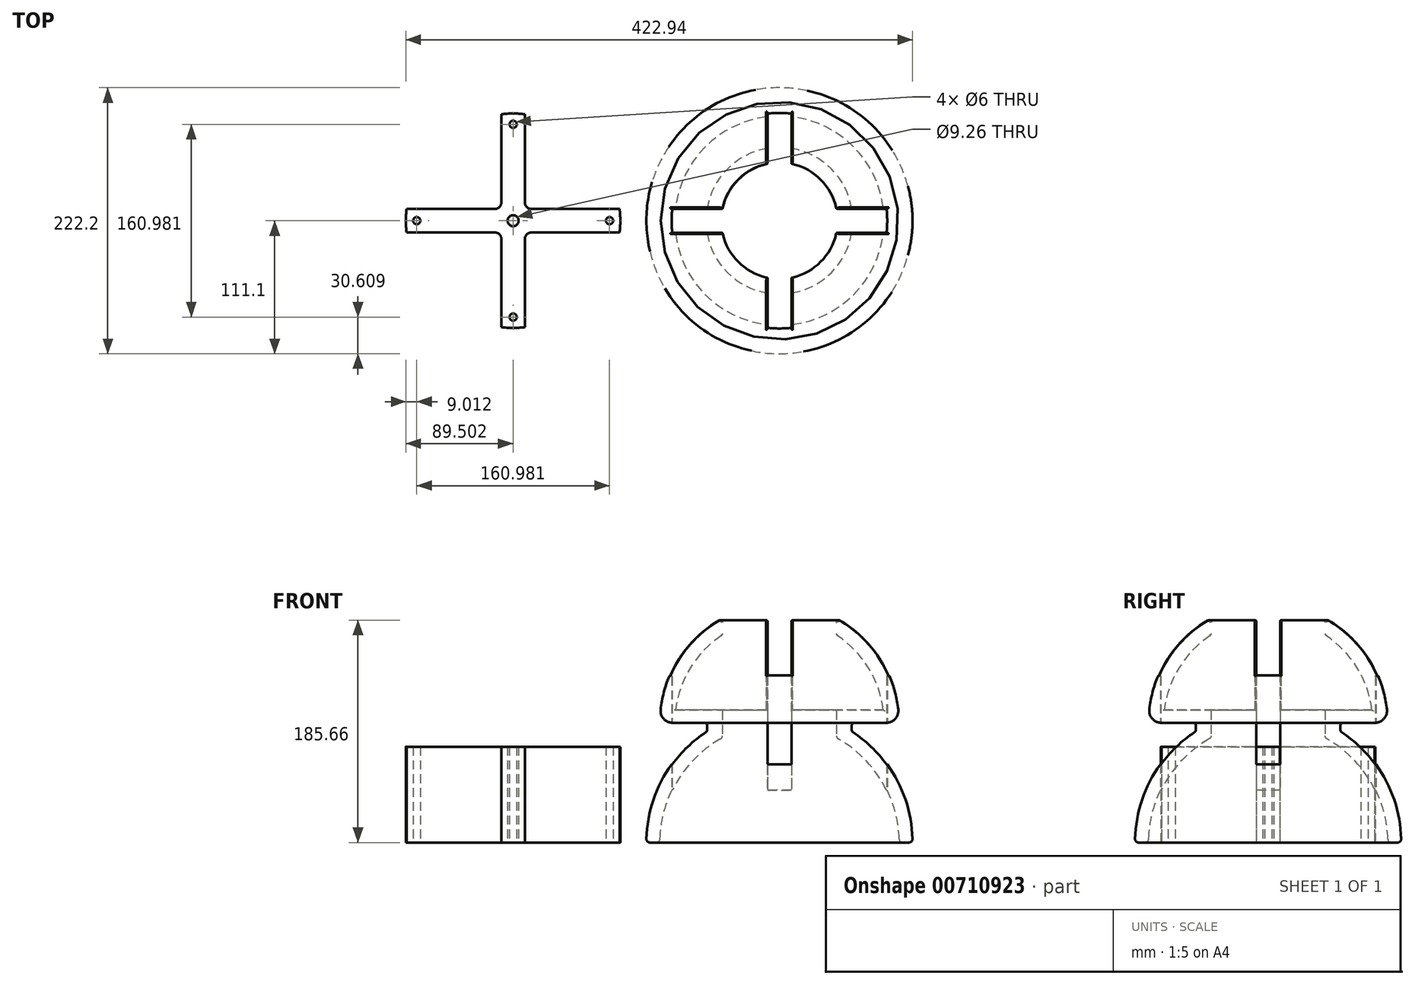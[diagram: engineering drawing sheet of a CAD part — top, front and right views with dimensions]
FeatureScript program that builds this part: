
annotation { "Feature Type Name" : "Feature", "Feature Type Description" : "" }
export const myFeature = defineFeature(function(context is Context, id is Id, definition is map)
    precondition{}
    {
        {
            var Q0;
            Q0=qCreatedBy(makeId("Front.planeOp"),FACE);
            var sketch = newSketch(context, id + "F0", { "sketchPlane" : qUnion([Q0])});
            skArc(sketch, "E0", {"start": v(100, 0) * mm, "mid": v(86.21, 50.67) * mm, "end": v(48.65, 87.37) * mm});
            skArc(sketch, "E1", {"start": v(111.14, 0) * mm, "mid": v(97.88, 52.66) * mm, "end": v(61.25, 92.74) * mm});
            skPoint(sketch, "E2", {"position": v(0, 100) * mm});
            skLineSegment(sketch, "E3", {"start": v(111.14, 0) * mm, "end": v(100, 0) * mm});
            skLineSegment(sketch, "E4", {"start": v(0, 0) * mm, "end": v(0, 246.19) * mm});
            skPoint(sketch, "E5.orphan", {"position": v(-88.06, 100) * mm});
            skPoint(sketch, "E6.orphan", {"position": v(-99.8, 100) * mm});
            skPoint(sketch, "E7.orphan", {"position": v(-111.14, 0) * mm});
            skPoint(sketch, "E8.orphan", {"position": v(-100, 0) * mm});
            skPoint(sketch, "E9.startSnap0", {"position": v(61.25, 144.4) * mm});
            skPoint(sketch, "E10.orphan", {"position": v(35.1, 144.4) * mm});
            skPoint(sketch, "E11.orphan", {"position": v(88.06, 100) * mm});
            skPoint(sketch, "E12.orphan", {"position": v(87.39, 144.4) * mm});
            skPoint(sketch, "E13.start.orphan", {"position": v(99.8, 100) * mm});
            skArc(sketch, "E14", {"start": v(99.2, 110.84) * mm, "mid": v(83.2, 155.13) * mm, "end": v(48.65, 187.14) * mm});
            skPoint(sketch, "E9.start.orphan", {"position": v(61.25, 133.56) * mm});
            skLineSegment(sketch, "E15", {"start": v(48.65, 87.37) * mm, "end": v(48.65, 110.84) * mm});
            skLineSegment(sketch, "E16", {"start": v(61.25, 92.74) * mm, "end": v(61.25, 100) * mm});
            skLineSegment(sketch, "E17", {"start": v(87.39, 110.84) * mm, "end": v(61.25, 110.84) * mm});
            skPoint(sketch, "E18.trimOffspring.end.orphan", {"position": v(-110.69, 100) * mm});
            skLineSegment(sketch, "E19", {"start": v(61.25, 110.84) * mm, "end": v(48.65, 110.84) * mm});
            skArc(sketch, "E20", {"start": v(87.39, 110.84) * mm, "mid": v(74.87, 146.36) * mm, "end": v(48.65, 173.4) * mm});
            skPoint(sketch, "E21.orphan", {"position": v(110.69, 100) * mm});
            skLineSegment(sketch, "E22", {"start": v(48.65, 187.14) * mm, "end": v(48.65, 173.4) * mm});
            skLineSegment(sketch, "E23", {"start": v(99.2, 110.84) * mm, "end": v(99.8, 100) * mm});
            skLineSegment(sketch, "E24", {"start": v(61.25, 100) * mm, "end": v(99.8, 100) * mm});
            skSolve(sketch);
        }
        {
            var Q0;
            Q0=makeQuery(id+"F0.imprint","IMPRINT",FACE,{"disambiguationData":[TD([[makeQuery(id+"F0.imprint","IMPRINT",EDGE,{"derivedFrom":sQuery(id+"F0.wireOp",EDGE,"E0")}),-1.0]])]});
            var Q1;
            Q1=sQuery(id+"F0.wireOp",EDGE,"E4");
            revolve(context, id + "F1", {"surfaceOperationType" : NewSurfaceOperationType.NEW, "entities" : qUnion([Q0]), "axis" : qUnion([Q1]), "revolveType" : RevolveType.FULL});
        }
        {
            var Q0;
            Q0=makeQuery(id+"F1.opRevolve","SWEPT_EDGE",EDGE,{"disambiguationData":[OSD([sQuery(id+"F0.wireOp",EDGE,"E20"),sQuery(id+"F0.wireOp",EDGE,"E22")])]});
            var Q1;
            Q1=makeQuery(id+"F1.opRevolve","SWEPT_EDGE",EDGE,{"disambiguationData":[OSD([sQuery(id+"F0.wireOp",EDGE,"E14"),sQuery(id+"F0.wireOp",EDGE,"E22")])]});
            fillet(context, id + "F2", {"entities" : qUnion([Q0, Q1]), "radius" : 2 * mm, "tangentPropagation" : true, "allowEdgeOverflow" : false});
        }
        {
            var Q0;
            Q0=makeQuery(id+"F1.opRevolve","SWEPT_FACE",FACE,{"disambiguationData":[OSD([sQuery(id+"F0.wireOp",EDGE,"E0")])]});
            var Q1;
            Q1=makeQuery(id+"F1.opRevolve","SWEPT_EDGE",EDGE,{"disambiguationData":[OSD([sQuery(id+"F0.wireOp",EDGE,"E1"),sQuery(id+"F0.wireOp",EDGE,"E3")])]});
            fillet(context, id + "F3", {"entities" : qUnion([Q0, Q1]), "radius" : 3 * mm, "tangentPropagation" : true, "allowEdgeOverflow" : false});
        }
        {
            var Q0;
            Q0=makeQuery(id+"F1.opRevolve","SWEPT_EDGE",EDGE,{"disambiguationData":[OSD([sQuery(id+"F0.wireOp",EDGE,"E16"),sQuery(id+"F0.wireOp",EDGE,"E24")])]});
            var Q1;
            Q1=makeQuery(id+"F1.opRevolve","SWEPT_EDGE",EDGE,{"disambiguationData":[OSD([sQuery(id+"F0.wireOp",EDGE,"E1"),sQuery(id+"F0.wireOp",EDGE,"E16")])]});
            fillet(context, id + "F4", {"entities" : qUnion([Q0, Q1]), "radius" : 2 * mm, "tangentPropagation" : true, "allowEdgeOverflow" : false});
        }
        {
            var Q0;
            Q0=qCreatedBy(makeId("Top.planeOp"),FACE);
            var sketch = newSketch(context, id + "F5", { "sketchPlane" : qUnion([Q0])});
            skArc(sketch, "E25", {"start": v(-89.44, 10) * mm, "mid": v(-90, 0) * mm, "end": v(-89.44, -10) * mm});
            skLineSegment(sketch, "E26", {"start": v(-10, -89.44) * mm, "end": v(-10, -10) * mm});
            skLineSegment(sketch, "E27", {"start": v(10, 89.44) * mm, "end": v(10, 10) * mm});
            skLineSegment(sketch, "E28", {"start": v(-89.44, 10) * mm, "end": v(-10, 10) * mm});
            skLineSegment(sketch, "E29", {"start": v(-89.44, -10) * mm, "end": v(-10, -10) * mm});
            skPoint(sketch, "E30.orphan", {"position": v(-59.43, -10) * mm});
            skPoint(sketch, "E31.orphan", {"position": v(10, -62.73) * mm});
            skPoint(sketch, "E32.orphan", {"position": v(-10, -60.97) * mm});
            skPoint(sketch, "E33.orphan", {"position": v(62.07, 10) * mm});
            skArc(sketch, "E34.trimOffspring", {"start": v(10, 89.44) * mm, "mid": v(0, 90) * mm, "end": v(-10, 89.44) * mm});
            skArc(sketch, "E35.trimOffspring", {"start": v(89.44, -10) * mm, "mid": v(90, 0) * mm, "end": v(89.44, 10) * mm});
            skArc(sketch, "E36.trimOffspring", {"start": v(-10, -89.44) * mm, "mid": v(0, -90) * mm, "end": v(10, -89.44) * mm});
            skLineSegment(sketch, "E37.trimOffspring", {"start": v(10, -10) * mm, "end": v(89.44, -10) * mm});
            skLineSegment(sketch, "E38.trimOffspring", {"start": v(10, 10) * mm, "end": v(89.44, 10) * mm});
            skLineSegment(sketch, "E39.trimOffspring", {"start": v(10, -10) * mm, "end": v(10, -89.44) * mm});
            skLineSegment(sketch, "E40.trimOffspring", {"start": v(-10, 10) * mm, "end": v(-10, 89.44) * mm});
            skSolve(sketch);
        }
        {
            var Q0;
            Q0=makeQuery(id+"F1.opRevolve","SWEPT_EDGE",EDGE,{"disambiguationData":[OSD([sQuery(id+"F0.wireOp",EDGE,"E23"),sQuery(id+"F0.wireOp",EDGE,"E24")])]});
            fillet(context, id + "F6", {"entities" : qUnion([Q0]), "radius" : 10 * mm, "tangentPropagation" : true, "allowEdgeOverflow" : false});
        }
        {
            var Q0;
            Q0=makeQuery(id+"F5.imprint","IMPRINT",FACE,{"disambiguationData":[TD([[makeQuery(id+"F5.imprint","IMPRINT",EDGE,{"derivedFrom":sQuery(id+"F5.wireOp",EDGE,"E25")}),1.0]])]});
            extrude(context, id + "F7", {"entities" : qUnion([Q0]), "operationType" : NewBodyOperationType.REMOVE, "depth" : 210 * mm, "offsetDistance" : 25 * mm});
        }
        {
            var Q0;
            Q0=makeQuery(id+"F7.boolean.opBoolean","INTERSECT",EDGE,{"derivedFrom":[makeQuery(id+"F1.opRevolve","SWEPT_FACE",FACE,{"disambiguationData":[OSD([sQuery(id+"F0.wireOp",EDGE,"E14")])]}),makeQuery(id+"F7.opExtrude","SWEPT_FACE",FACE,{"disambiguationData":[OSD([sQuery(id+"F5.wireOp",EDGE,"E25")])]})]});
            var Q1;
            Q1=makeQuery(id+"F7.boolean.opBoolean","INTERSECT",EDGE,{"derivedFrom":[makeQuery(id+"F1.opRevolve","SWEPT_FACE",FACE,{"disambiguationData":[OSD([sQuery(id+"F0.wireOp",EDGE,"E14")])]}),makeQuery(id+"F7.opExtrude","SWEPT_FACE",FACE,{"disambiguationData":[OSD([sQuery(id+"F5.wireOp",EDGE,"E28")])]})]});
            var Q2;
            Q2=makeQuery(id+"F1.opRevolve","SWEPT_FACE",FACE,{"disambiguationData":[OSD([sQuery(id+"F0.wireOp",EDGE,"E14")])]});
            var Q3;
            Q3=makeQuery(id+"F7.boolean.opBoolean","INTERSECT",EDGE,{"derivedFrom":[makeQuery(id+"F1.opRevolve","SWEPT_FACE",FACE,{"disambiguationData":[OSD([sQuery(id+"F0.wireOp",EDGE,"E17"),sQuery(id+"F0.wireOp",EDGE,"E19")])]}),makeQuery(id+"F7.opExtrude","SWEPT_FACE",FACE,{"disambiguationData":[OSD([sQuery(id+"F5.wireOp",EDGE,"E40.trimOffspring")])]})]});
            var Q4;
            Q4=makeQuery(id+"F7.boolean.opBoolean","INTERSECT",EDGE,{"derivedFrom":[makeQuery(id+"F1.opRevolve","SWEPT_FACE",FACE,{"disambiguationData":[OSD([sQuery(id+"F0.wireOp",EDGE,"E17"),sQuery(id+"F0.wireOp",EDGE,"E19")])]}),makeQuery(id+"F7.opExtrude","SWEPT_FACE",FACE,{"disambiguationData":[OSD([sQuery(id+"F5.wireOp",EDGE,"E34.trimOffspring")])]})]});
            var Q5;
            Q5=makeQuery(id+"F7.boolean.opBoolean","INTERSECT",EDGE,{"derivedFrom":[makeQuery(id+"F1.opRevolve","SWEPT_FACE",FACE,{"disambiguationData":[OSD([sQuery(id+"F0.wireOp",EDGE,"E17"),sQuery(id+"F0.wireOp",EDGE,"E19")])]}),makeQuery(id+"F7.opExtrude","SWEPT_FACE",FACE,{"disambiguationData":[OSD([sQuery(id+"F5.wireOp",EDGE,"E27")])]})]});
            var Q6;
            {var subQ0=sQuery(id+"F0.wireOp",EDGE,"E15");var subQ1=sQuery(id+"F0.wireOp",EDGE,"E19");Q6=makeQuery(id+"F7.boolean.opBoolean","SPLIT",EDGE,{"disambiguationData":[TD([makeQuery(id+"F7.opExtrude","SWEPT_FACE",FACE,{"disambiguationData":[OSD([sQuery(id+"F5.wireOp",EDGE,"E27")])]})])],"derivedFrom":makeQuery(id+"F1.opRevolve","SWEPT_EDGE",EDGE,{"disambiguationData":[OSD([subQ0,subQ1])]})});}
            var Q7;
            {var subQ0=sQuery(id+"F0.wireOp",EDGE,"E15");var subQ1=sQuery(id+"F0.wireOp",EDGE,"E19");Q7=makeQuery(id+"F7.boolean.opBoolean","SPLIT",EDGE,{"disambiguationData":[TD([makeQuery(id+"F7.opExtrude","SWEPT_FACE",FACE,{"disambiguationData":[OSD([sQuery(id+"F5.wireOp",EDGE,"E28")])]})])],"derivedFrom":makeQuery(id+"F1.opRevolve","SWEPT_EDGE",EDGE,{"disambiguationData":[OSD([subQ0,subQ1])]})});}
            var Q8;
            Q8=makeQuery(id+"F7.boolean.opBoolean","INTERSECT",EDGE,{"derivedFrom":[makeQuery(id+"F1.opRevolve","SWEPT_FACE",FACE,{"disambiguationData":[OSD([sQuery(id+"F0.wireOp",EDGE,"E17"),sQuery(id+"F0.wireOp",EDGE,"E19")])]}),makeQuery(id+"F7.opExtrude","SWEPT_FACE",FACE,{"disambiguationData":[OSD([sQuery(id+"F5.wireOp",EDGE,"E36.trimOffspring")])]})]});
            var Q9;
            {var subQ0=sQuery(id+"F5.wireOp",EDGE,"E26");var subQ1=sQuery(id+"F5.wireOp",EDGE,"E36.trimOffspring");Q9=makeQuery(id+"F7.boolean.opBoolean","COPY",EDGE,{"disambiguationData":[TD([makeQuery(id+"F1.opRevolve","SWEPT_FACE",FACE,{"disambiguationData":[OSD([sQuery(id+"F0.wireOp",EDGE,"E0")])]})])],"derivedFrom":makeQuery(id+"F7.opExtrude","SWEPT_EDGE",EDGE,{"disambiguationData":[OSD([subQ0,subQ1])]})});}
            var Q10;
            {var subQ0=sQuery(id+"F0.wireOp",EDGE,"E15");var subQ1=sQuery(id+"F0.wireOp",EDGE,"E19");Q10=makeQuery(id+"F7.boolean.opBoolean","SPLIT",EDGE,{"disambiguationData":[TD([makeQuery(id+"F7.opExtrude","SWEPT_FACE",FACE,{"disambiguationData":[OSD([sQuery(id+"F5.wireOp",EDGE,"E26")])]})])],"derivedFrom":makeQuery(id+"F1.opRevolve","SWEPT_EDGE",EDGE,{"disambiguationData":[OSD([subQ0,subQ1])]})});}
            var Q11;
            {var subQ0=sQuery(id+"F0.wireOp",EDGE,"E15");var subQ1=sQuery(id+"F0.wireOp",EDGE,"E19");Q11=makeQuery(id+"F7.boolean.opBoolean","SPLIT",EDGE,{"disambiguationData":[TD([makeQuery(id+"F7.opExtrude","SWEPT_FACE",FACE,{"disambiguationData":[OSD([sQuery(id+"F5.wireOp",EDGE,"E37.trimOffspring")])]})])],"derivedFrom":makeQuery(id+"F1.opRevolve","SWEPT_EDGE",EDGE,{"disambiguationData":[OSD([subQ0,subQ1])]})});}
            var Q12;
            Q12=makeQuery(id+"F7.boolean.opBoolean","INTERSECT",EDGE,{"derivedFrom":[makeQuery(id+"F1.opRevolve","SWEPT_FACE",FACE,{"disambiguationData":[OSD([sQuery(id+"F0.wireOp",EDGE,"E17"),sQuery(id+"F0.wireOp",EDGE,"E19")])]}),makeQuery(id+"F7.opExtrude","SWEPT_FACE",FACE,{"disambiguationData":[OSD([sQuery(id+"F5.wireOp",EDGE,"E35.trimOffspring")])]})]});
            var Q13;
            Q13=makeQuery(id+"F7.boolean.opBoolean","INTERSECT",EDGE,{"derivedFrom":[makeQuery(id+"F1.opRevolve","SWEPT_FACE",FACE,{"disambiguationData":[OSD([sQuery(id+"F0.wireOp",EDGE,"E17"),sQuery(id+"F0.wireOp",EDGE,"E19")])]}),makeQuery(id+"F7.opExtrude","SWEPT_FACE",FACE,{"disambiguationData":[OSD([sQuery(id+"F5.wireOp",EDGE,"E38.trimOffspring")])]})]});
            var Q14;
            Q14=makeQuery(id+"F7.boolean.opBoolean","INTERSECT",EDGE,{"derivedFrom":[makeQuery(id+"F1.opRevolve","SWEPT_FACE",FACE,{"disambiguationData":[OSD([sQuery(id+"F0.wireOp",EDGE,"E17"),sQuery(id+"F0.wireOp",EDGE,"E19")])]}),makeQuery(id+"F7.opExtrude","SWEPT_FACE",FACE,{"disambiguationData":[OSD([sQuery(id+"F5.wireOp",EDGE,"E37.trimOffspring")])]})]});
            fillet(context, id + "F8", {"entities" : qUnion([Q0, Q1, Q2, Q3, Q4, Q5, Q6, Q7, Q8, Q9, Q10, Q11, Q12, Q13, Q14]), "radius" : 1 * mm, "tangentPropagation" : true, "allowEdgeOverflow" : false});
        }
        {
            var Q0;
            Q0=makeQuery(id+"F5.imprint","IMPRINT",FACE,{"disambiguationData":[TD([[makeQuery(id+"F5.imprint","IMPRINT",EDGE,{"derivedFrom":sQuery(id+"F5.wireOp",EDGE,"E25")}),1.0]])]});
            var sketch = newSketch(context, id + "F9", { "sketchPlane" : qUnion([Q0])});
            skPoint(sketch, "E41", {"position": v(-222.34, 0) * mm});
            skArc(sketch, "E42", {"start": v(-212.44, 88.95) * mm, "mid": v(-222.34, 89.5) * mm, "end": v(-232.24, 88.95) * mm});
            skLineSegment(sketch, "E43", {"start": v(-212.44, 88.95) * mm, "end": v(-212.44, 14.86) * mm});
            skLineSegment(sketch, "E44", {"start": v(-232.24, -88.95) * mm, "end": v(-232.24, -14.9) * mm});
            skLineSegment(sketch, "E45", {"start": v(-311.3, 9.86) * mm, "end": v(-237.24, 9.86) * mm});
            skArc(sketch, "E46.trimOffspring", {"start": v(-133.39, -9.9) * mm, "mid": v(-132.84, -0.02) * mm, "end": v(-133.38, 9.86) * mm});
            skArc(sketch, "E47.trimOffspring", {"start": v(-232.24, -88.95) * mm, "mid": v(-222.34, -89.5) * mm, "end": v(-212.44, -88.95) * mm});
            skArc(sketch, "E48.trimOffspring", {"start": v(-311.3, 9.86) * mm, "mid": v(-311.84, -0.02) * mm, "end": v(-311.29, -9.9) * mm});
            skPoint(sketch, "E49.orphan", {"position": v(-222.34, -97.04) * mm});
            skPoint(sketch, "E50.orphan", {"position": v(-122.77, -9.9) * mm});
            skPoint(sketch, "E51.orphan", {"position": v(-124.04, 0) * mm});
            skPoint(sketch, "E52.orphan", {"position": v(-124.88, 9.86) * mm});
            skPoint(sketch, "E53.orphan", {"position": v(-222.34, 98.72) * mm});
            skPoint(sketch, "E54.orphan", {"position": v(-334.14, -9.9) * mm});
            skPoint(sketch, "E55.orphan", {"position": v(-334.56, 0) * mm});
            skLineSegment(sketch, "E56.trimOffspring", {"start": v(-207.44, 9.86) * mm, "end": v(-133.38, 9.86) * mm});
            skLineSegment(sketch, "E57.trimOffspring", {"start": v(-207.44, -9.9) * mm, "end": v(-133.39, -9.9) * mm});
            skLineSegment(sketch, "E58", {"start": v(-311.29, -9.9) * mm, "end": v(-237.24, -9.9) * mm});
            skLineSegment(sketch, "E59.trimOffspring", {"start": v(-232.24, 14.86) * mm, "end": v(-232.24, 88.95) * mm});
            skLineSegment(sketch, "E60.trimOffspring", {"start": v(-212.44, -14.9) * mm, "end": v(-212.44, -88.95) * mm});
            skPoint(sketch, "E61.end.orphan", {"position": v(-217.28, 0) * mm});
            skLineSegment(sketch, "E62", {"start": v(-222.34, 80.5) * mm, "end": v(-222.34, 83.5) * mm, "construction": true});
            skArc(sketch, "E63", {"start": v(-219.34, 80.43) * mm, "mid": v(-220.84, 80.48) * mm, "end": v(-222.34, 80.5) * mm, "construction": true});
            skCircle(sketch, "E64", {"center": v(-222.34, 80.5) * mm, "radius": 3 * mm});
            skCircle(sketch, "E65", {"center": v(-302.83, 0) * mm, "radius": 3 * mm});
            skCircle(sketch, "E66", {"center": v(-222.34, -80.5) * mm, "radius": 3 * mm});
            skCircle(sketch, "E67", {"center": v(-141.85, 0) * mm, "radius": 3 * mm});
            skArc(sketch, "E68.trimOffspring", {"start": v(-141.9, -3) * mm, "mid": v(-141.86, -1.5) * mm, "end": v(-141.85, 0) * mm, "construction": true});
            skArc(sketch, "E69.trimOffspring", {"start": v(-302.77, 3) * mm, "mid": v(-302.81, 1.5) * mm, "end": v(-302.83, 0) * mm, "construction": true});
            skLineSegment(sketch, "E70.trimOffspring", {"start": v(-222.34, 0) * mm, "end": v(-217.28, 0) * mm, "construction": true});
            skLineSegment(sketch, "E71.trimOffspring", {"start": v(-144.85, 0) * mm, "end": v(-141.85, 0) * mm, "construction": true});
            skLineSegment(sketch, "E72.trimOffspring", {"start": v(-305.83, 0) * mm, "end": v(-302.83, 0) * mm, "construction": true});
            skLineSegment(sketch, "E73.trimOffspring", {"start": v(-222.34, 83.5) * mm, "end": v(-222.34, 80.5) * mm, "construction": true});
            skPoint(sketch, "E74.visualSharp", {"position": v(-232.24, 9.86) * mm});
            skArc(sketch, "E74.filletArc", {"start": v(-237.24, 9.86) * mm, "mid": v(-233.7, 11.33) * mm, "end": v(-232.24, 14.86) * mm});
            skPoint(sketch, "E75.visualSharp", {"position": v(-212.44, 9.86) * mm});
            skArc(sketch, "E75.filletArc", {"start": v(-212.44, 14.86) * mm, "mid": v(-210.97, 11.33) * mm, "end": v(-207.44, 9.86) * mm});
            skPoint(sketch, "E76.visualSharp", {"position": v(-212.44, -9.9) * mm});
            skArc(sketch, "E76.filletArc", {"start": v(-207.44, -9.9) * mm, "mid": v(-210.97, -11.36) * mm, "end": v(-212.44, -14.9) * mm});
            skPoint(sketch, "E77.visualSharp", {"position": v(-232.24, -9.9) * mm});
            skArc(sketch, "E77.filletArc", {"start": v(-232.24, -14.9) * mm, "mid": v(-233.7, -11.36) * mm, "end": v(-237.24, -9.9) * mm});
            skCircle(sketch, "E78", {"center": v(-222.34, 0) * mm, "radius": 4.63 * mm});
            skSolve(sketch);
        }
        {
            var Q0;
            Q0=makeQuery(id+"F9.imprint","IMPRINT",FACE,{"disambiguationData":[TD([[makeQuery(id+"F9.imprint","IMPRINT",EDGE,{"derivedFrom":sQuery(id+"F9.wireOp",EDGE,"E42")}),1.0]])]});
            extrude(context, id + "F10", {"entities" : qUnion([Q0]), "depth" : 80 * mm, "offsetDistance" : 25 * mm});
        }
    });
